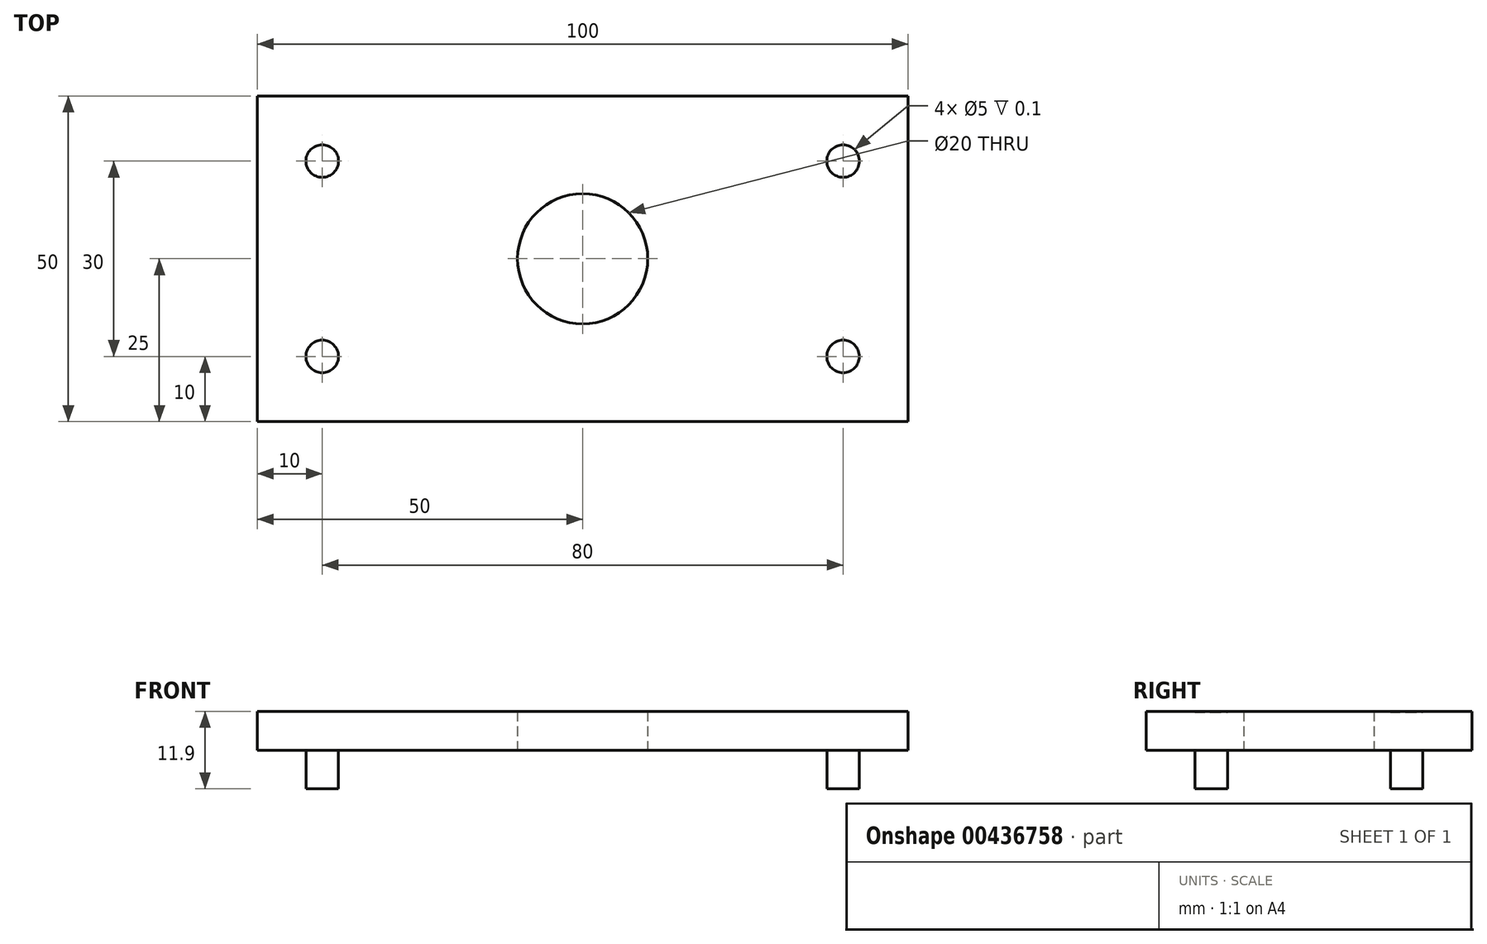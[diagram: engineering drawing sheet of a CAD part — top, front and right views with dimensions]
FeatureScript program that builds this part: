
annotation { "Feature Type Name" : "Feature", "Feature Type Description" : "" }
export const myFeature = defineFeature(function(context is Context, id is Id, definition is map)
    precondition{}
    {
        {
            var Q0;
            Q0=qCreatedBy(makeId("Top.planeOp"),FACE);
            var sketch = newSketch(context, id + "F0", { "sketchPlane" : qUnion([Q0])});
            skLineSegment(sketch, "E0.bottom", {"start": v(-50, -25) * mm, "end": v(50, -25) * mm});
            skLineSegment(sketch, "E0.top", {"start": v(-50, 25) * mm, "end": v(50, 25) * mm});
            skLineSegment(sketch, "E0.left", {"start": v(-50, -25) * mm, "end": v(-50, 25) * mm});
            skLineSegment(sketch, "E0.right", {"start": v(50, -25) * mm, "end": v(50, 25) * mm});
            skPoint(sketch, "E0.middle", {"position": v(0, 0) * mm});
            skLineSegment(sketch, "E1.0", {"start": v(-45, -20) * mm, "end": v(45, -20) * mm});
            skLineSegment(sketch, "E1.1", {"start": v(-45, -20) * mm, "end": v(-45, 20) * mm});
            skLineSegment(sketch, "E1.2", {"start": v(-45, 20) * mm, "end": v(45, 20) * mm});
            skLineSegment(sketch, "E1.3", {"start": v(45, -20) * mm, "end": v(45, 20) * mm});
            skLineSegment(sketch, "E2", {"start": v(-35, -20) * mm, "end": v(-35, -10) * mm});
            skLineSegment(sketch, "E3", {"start": v(-35, -10) * mm, "end": v(-45, -10) * mm});
            skLineSegment(sketch, "E4", {"start": v(-45, 10) * mm, "end": v(-35, 10) * mm});
            skLineSegment(sketch, "E5", {"start": v(-35, 10) * mm, "end": v(-35, 20) * mm});
            skLineSegment(sketch, "E6", {"start": v(35, 20) * mm, "end": v(35, 10) * mm});
            skLineSegment(sketch, "E7", {"start": v(35, 10) * mm, "end": v(45, 10) * mm});
            skLineSegment(sketch, "E8", {"start": v(35, -20) * mm, "end": v(35, -10) * mm});
            skLineSegment(sketch, "E9", {"start": v(35, -10) * mm, "end": v(45, -10) * mm});
            skPoint(sketch, "E10", {"position": v(-40, -15) * mm});
            skPoint(sketch, "E10.positionSnap0", {"position": v(-40, -10) * mm});
            skPoint(sketch, "E10.positionSnap1", {"position": v(-35, -15) * mm});
            skPoint(sketch, "E11", {"position": v(40, -15) * mm});
            skPoint(sketch, "E11.positionSnap0", {"position": v(35, -15) * mm});
            skPoint(sketch, "E11.positionSnap1", {"position": v(40, -10) * mm});
            skPoint(sketch, "E12", {"position": v(40, 15) * mm});
            skPoint(sketch, "E12.positionSnap0", {"position": v(35, 15) * mm});
            skPoint(sketch, "E13", {"position": v(-40, 15) * mm});
            skPoint(sketch, "E13.positionSnap0", {"position": v(-35, 15) * mm});
            skPoint(sketch, "E13.positionSnap1", {"position": v(-40, 10) * mm});
            skCircle(sketch, "E14", {"center": v(-40, -15) * mm, "radius": 2.5 * mm});
            skCircle(sketch, "E15", {"center": v(40, -15) * mm, "radius": 2.5 * mm});
            skCircle(sketch, "E16", {"center": v(40, 15) * mm, "radius": 2.5 * mm});
            skCircle(sketch, "E17", {"center": v(-40, 15) * mm, "radius": 2.5 * mm});
            skCircle(sketch, "E18", {"center": v(0, 0) * mm, "radius": 10 * mm});
            skSolve(sketch);
        }
        {
            var Q0;
            {var subQ4=sQuery(id+"F0.wireOp",EDGE,"E2");Q0=makeQuery(id+"F0.imprint","IMPRINT",FACE,{"disambiguationData":[TD([[makeQuery(id+"F0.imprint","IMPRINT",EDGE,{"derivedFrom":subQ4}),-1.0]])]});}
            var Q1;
            Q1=makeQuery(id+"F0.imprint","IMPRINT",FACE,{"disambiguationData":[TD([[makeQuery(id+"F0.imprint","IMPRINT",EDGE,{"derivedFrom":sQuery(id+"F0.wireOp",EDGE,"E0.bottom")}),1.0]])]});
            var Q2;
            {var subQ0=sQuery(id+"F0.wireOp",EDGE,"E2");Q2=makeQuery(id+"F0.imprint","IMPRINT",FACE,{"disambiguationData":[TD([[makeQuery(id+"F0.imprint","IMPRINT",EDGE,{"derivedFrom":subQ0}),1.0]])]});}
            var Q3;
            {var subQ0=sQuery(id+"F0.wireOp",EDGE,"E4");Q3=makeQuery(id+"F0.imprint","IMPRINT",FACE,{"disambiguationData":[TD([[makeQuery(id+"F0.imprint","IMPRINT",EDGE,{"derivedFrom":subQ0}),1.0]])]});}
            var Q4;
            {var subQ0=sQuery(id+"F0.wireOp",EDGE,"E8");Q4=makeQuery(id+"F0.imprint","IMPRINT",FACE,{"disambiguationData":[TD([[makeQuery(id+"F0.imprint","IMPRINT",EDGE,{"derivedFrom":subQ0}),-1.0]])]});}
            var Q5;
            {var subQ1=sQuery(id+"F0.wireOp",EDGE,"E6");Q5=makeQuery(id+"F0.imprint","IMPRINT",FACE,{"disambiguationData":[TD([[makeQuery(id+"F0.imprint","IMPRINT",EDGE,{"derivedFrom":subQ1}),1.0]])]});}
            extrude(context, id + "F1", {"entities" : qUnion([Q0, Q1, Q2, Q3, Q4, Q5]), "depth" : 6 * mm});
        }
        {
            var Q0;
            Q0=makeQuery(id+"F0.imprint","IMPRINT",FACE,{"disambiguationData":[TD([[makeQuery(id+"F0.imprint","IMPRINT",EDGE,{"derivedFrom":sQuery(id+"F0.wireOp",EDGE,"E14")}),1.0]])]});
            var Q1;
            Q1=makeQuery(id+"F0.imprint","IMPRINT",FACE,{"disambiguationData":[TD([[makeQuery(id+"F0.imprint","IMPRINT",EDGE,{"derivedFrom":sQuery(id+"F0.wireOp",EDGE,"E16")}),1.0]])]});
            var Q2;
            Q2=makeQuery(id+"F0.imprint","IMPRINT",FACE,{"disambiguationData":[TD([[makeQuery(id+"F0.imprint","IMPRINT",EDGE,{"derivedFrom":sQuery(id+"F0.wireOp",EDGE,"E17")}),1.0]])]});
            var Q3;
            Q3=makeQuery(id+"F0.imprint","IMPRINT",FACE,{"disambiguationData":[TD([[makeQuery(id+"F0.imprint","IMPRINT",EDGE,{"derivedFrom":sQuery(id+"F0.wireOp",EDGE,"E15")}),1.0]])]});
            extrude(context, id + "F2", {"entities" : qUnion([Q0, Q1, Q2, Q3]), "operationType" : NewBodyOperationType.ADD, "endBound" : BoundingType.SYMMETRIC, "depth" : 11.8 * mm});
        }
    });
